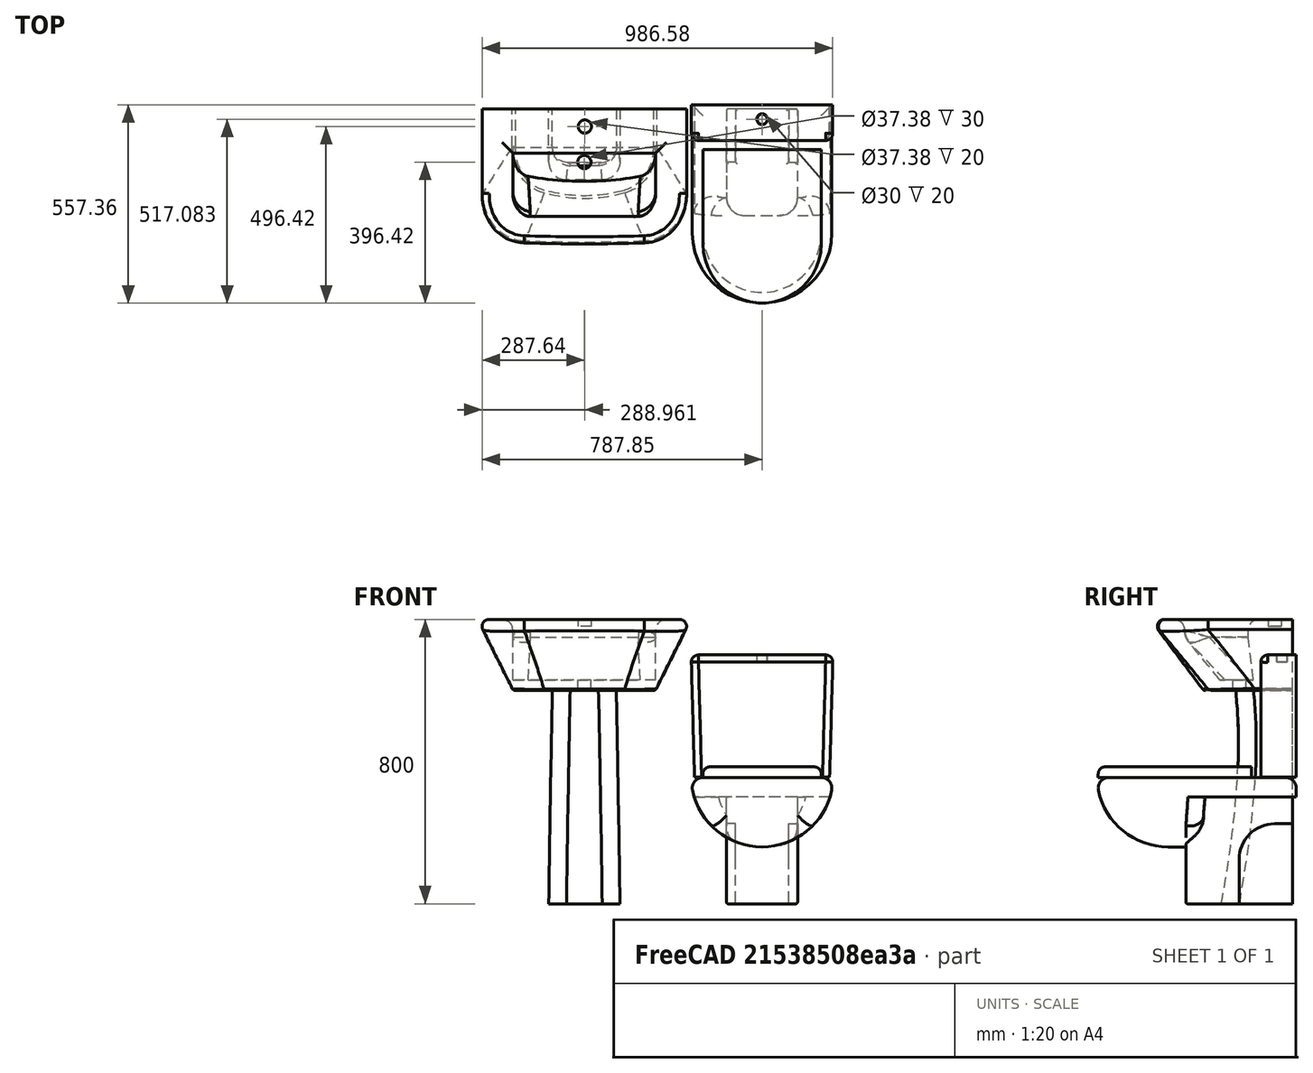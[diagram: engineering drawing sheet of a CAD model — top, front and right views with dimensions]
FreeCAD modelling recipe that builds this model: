
FCSTD DOCUMENT  (FreeCAD 0.16R6706 (Git))
Label: bathroom
License: All rights reserved
LicenseURL: http://en.wikipedia.org/wiki/All_rights_reserved
objects: Part::Fillet×15, Part::Cut×10, Part::Feature×8, Part::Part2DObjectPython×7, Part::Extrusion×6, Part::MultiFuse×4, Part::Loft×3, Part::FeaturePython×2, Part::Mirroring×1
note: 56 computed .brp shape members not serialized (recipe doc carries the construction recipe); baked Part::Feature solids carry a one-line shape summary decoded from their .brp

FEATURE [Part::Cut] Cut
  Placement = pos=(0,0,380) rot=(0,0,1;0rad)
FEATURE [Part::Feature] Extrusion003
  Placement = pos=(0.311371,-200,244.366) rot=(0,0,1;0rad)
  shape: bbox 600 x 300 x 243.1 mm, 6 faces (baked)
FEATURE [Part::Cut] Cut002
  Base = -> Cut
  Tool = -> Extrusion003
FEATURE [Part::Feature] Face
  shape: bbox 399.9 x 2e-07 x 195.3 mm, 1 faces, 0 solids (baked)
FEATURE [Part::Extrusion] Extrusion
  Base = -> Face
  Dir = (0,360.459,0)
  Solid = true
FEATURE [Part::MultiFuse] Fusion
  Placement = pos=(0,0,-400) rot=(0,0,1;0rad)
  Shapes = -> [Cut002,Extrusion]
FEATURE [Part::Cut] Cut003
  Base = -> Fusion
FEATURE [Part::Fillet] Fillet001
  Base = -> Cut003
  Edges = 4 edges r=50: [Edge8,Edge9,Edge15,Edge16]
FEATURE [Part::Part2DObjectPython] Rectangle001  # Draft 2D object (typed FeaturePython)
  ChamferSize = 0
  Columns = 1
  FilletRadius = 0
  Height = 300
  Length = 200
  MakeFace = true
  Placement = pos=(-100,50,0) rot=(0,0,1;0rad)
  Rows = 1
FEATURE [Part::Extrusion] Extrusion004
  Base = -> Rectangle001
  Dir = (0,0,300)
  Solid = true
FEATURE [Part::Fillet] Fillet
  Base = -> Extrusion004
  Edges = 2 edges r=50: [Edge1,Edge2]
FEATURE [Part::Fillet] Fillet002
  Base = -> Fillet001
  Edges = 4 edges r=30: [Edge5,Edge13,Edge21,Edge26]
FEATURE [Part::Fillet] Fillet003
  Base = -> Fillet
  Edges = 2 edges r=5: [Edge17,Edge18]
FEATURE [Part::Part2DObjectPython] Rectangle005  # Draft 2D object (typed FeaturePython)
  ChamferSize = 0
  Columns = 1
  FilletRadius = 0
  Height = 100
  Length = 380
  MakeFace = true
  Placement = pos=(-190,260.943,355.887) rot=(0,0,1;0rad)
  Rows = 1
FEATURE [Part::Part2DObjectPython] Clone2D  label="Clone of Rectangle005 (2D)"  # Draft 2D object (typed FeaturePython)
  Objects = -> [Rectangle005]
  Placement = pos=(-190,260.943,700) rot=(0,0,1;0rad)
  Scale = (1.05,1,1)
FEATURE [Part::Loft] Loft
  Closed = false
  Ruled = false
  Sections = -> [Rectangle005,Clone2D]
  Solid = true
FEATURE [Part::Fillet] Fillet004
  Base = -> Loft
  Edges = 2 edges r=20: [Edge2,Edge4]
FEATURE [Part::Fillet] Fillet005
  Base = -> Fillet004
  Edges = 5 edges r=20: [Edge4,Edge11,Edge13,Edge14,Edge15]
FEATURE [Part::Part2DObjectPython] Rectangle006  # Draft 2D object (typed FeaturePython)
  ChamferSize = 0
  Columns = 1
  FilletRadius = 0
  Height = 200
  Length = 100
  MakeFace = true
  Placement = pos=(200,200,0) rot=(0,0,1;0rad)
  Rows = 1
FEATURE [Part::Extrusion] Extrusion005
  Base = -> Rectangle006
  Dir = (0,0,225)
  Solid = true
FEATURE [Part::Fillet] Fillet006
  Base = -> Extrusion005
  Edges = 1 edges r=100: [Edge4]
  Placement = pos=(-125,0,0) rot=(0,0,1;0rad)
FEATURE [Part::Mirroring] mirror  label="Mirror of Clone of Fillet006"
  Base = (0,500,0)
  Normal = (-1,0,0)
FEATURE [Part::Cut] Cut004
  Base = -> Fillet003
  Tool = -> Fillet006
FEATURE [Part::Cut] Cut005
  Base = -> Cut004
  Tool = -> mirror
FEATURE [Part::Fillet] Fillet007
  Base = -> Cut005
  Edges = 10 edges r=5: [Edge1,Edge2,Edge3,Edge4,Edge5,Edge6,Edge7,Edge8,Edge9,Edge10]
FEATURE [Part::Feature] Wire
  shape: bbox 332.8 x 434.2 x 2e-07 mm, 0 faces, 0 solids (baked)
FEATURE [Part::FeaturePython] Clone001  label="Clone of Wire"  # Draft clone (typed FeaturePython)
  Objects = -> [Wire]
  Placement = pos=(0,0,30) rot=(0,0,1;0rad)
  Scale = (1,1,1)
FEATURE [Part::Loft] Loft001
  Closed = false
  Ruled = false
  Sections = -> [Wire,Clone001]
  Solid = true
FEATURE [Part::Fillet] Fillet008
  Base = -> Loft001
  Edges = 1 edges r=20: [Edge7]
  Placement = pos=(0,970,-50) rot=(0,0,1;0rad)
FEATURE [Part::Part2DObjectPython] Circle  # Draft 2D object (typed FeaturePython)
  FirstAngle = 0
  LastAngle = 0
  MakeFace = true
  Placement = pos=(0.210445,320.663,700) rot=(0,0,1;0rad)
  Radius = 15
FEATURE [Part::Extrusion] Extrusion006
  Base = -> Circle
  Dir = (0,0,20)
  Placement = pos=(0,0,-20) rot=(0,0,1;0rad)
  Solid = true
FEATURE [Part::FeaturePython] Clone  label="Clone of Extrusion006"  # Draft clone (typed FeaturePython)
  Objects = -> [Extrusion006]
  Placement = pos=(0,9.5,-20) rot=(0,0,1;0rad)
  Scale = (0.97,0.97,1)
FEATURE [Part::Cut] Cut006
  Base = -> Fillet005
  Tool = -> Extrusion006
FEATURE [Part::MultiFuse] Fusion001  label="vaso_s"
  Placement = pos=(500,0,0) rot=(0,0,1;0rad)
  Shapes = -> [Cut006,Clone,Fillet008,Fillet007,Fillet002]
FEATURE [Part::Part2DObjectPython] Rectangle007  # Draft 2D object (typed FeaturePython)
  ChamferSize = 0
  Columns = 1
  FilletRadius = 0
  Height = -100
  Length = -400
  MakeFace = true
  Placement = pos=(200,200,0) rot=(0,0,1;0rad)
  Rows = 1
FEATURE [Part::Extrusion] Extrusion007
  Base = -> Rectangle007
  Dir = (0,0,786.749)
  Solid = true
FEATURE [Part::Cut] Cut007
  Tool = -> Extrusion007
FEATURE [Part::Fillet] Fillet009  label="coluna"
  Base = -> Cut007
  Edges = 2 edges r=50: [Edge8,Edge11]
FEATURE [Part::Part2DObjectPython] Rectangle002  # Draft 2D object (typed FeaturePython)
  ChamferSize = 0
  Columns = 1
  FilletRadius = 0
  Height = -400
  Length = 600
  MakeFace = true
  Placement = pos=(-300,100,800) rot=(0,0,1;0rad)
  Rows = 1
FEATURE [Part::Feature] Face001
  Placement = pos=(0,0,600) rot=(0,0,1;0rad)
  shape: bbox 400 x 268.8 x 2e-07 mm, 1 faces, 0 solids (baked)
FEATURE [Part::Loft] Loft002
  Closed = false
  Ruled = false
  Sections = -> [Face001,Rectangle002]
  Solid = true
FEATURE [Part::Fillet] Fillet010
  Base = -> Loft002
  Edges = 2 edges r=150: [Edge2,Edge4]
FEATURE [Part::Fillet] Fillet011
  Base = -> Fillet010
  Edges = 5 edges r=20: [Edge4,Edge11,Edge13,Edge14,Edge15]
FEATURE [Part::Fillet] Fillet012  label="lavat"
  Base = -> Fillet011
  Edges = 5 edges r=10: [Edge3,Edge6,Edge11,Edge12,Edge13]
FEATURE [Part::Feature] Solid
  shape: bbox 402.1 x 200.6 x 205.9 mm, 8 faces (baked)
FEATURE [Part::Feature] Face002
  shape: bbox 402.1 x 178.5 x 0.002 mm, 1 faces, 0 solids (baked)
FEATURE [Part::Extrusion] Extrusion001
  Base = -> Face002
  Dir = (0,0,327.541)
  Solid = true
FEATURE [Part::MultiFuse] Fusion002
  Shapes = -> [Solid,Extrusion001]
FEATURE [Part::Fillet] Fillet013
  Base = -> Fusion002
  Edges = 5 edges r=50: [Edge8,Edge10,Edge14,Edge17,Edge18]
  Placement = pos=(0,0,-170) rot=(0,0,1;0rad)
FEATURE [Part::Cut] Cut001
  Base = -> Fillet012
  Tool = -> Fillet013
FEATURE [Part::Fillet] Fillet014
  Base = -> Cut001
  Edges = 6 edges r=30: [Edge33,Edge34,Edge35,Edge36,Edge37,Edge38]
FEATURE [Part::Feature] Extrusion008
  Placement = pos=(1.32089,450,780) rot=(0,0,1;0rad)
  shape: bbox 37.38 x 37.38 x 68.11 mm, 3 faces (baked)
FEATURE [Part::Cut] Cut008
  Base = -> Fillet014
  Tool = -> Extrusion008
FEATURE [Part::Feature] Extrusion009
  Placement = pos=(0,350,590) rot=(0,0,1;0rad)
  shape: bbox 37.38 x 37.38 x 68.11 mm, 3 faces (baked)
FEATURE [Part::Cut] Cut009
  Base = -> Cut008
  Tool = -> Extrusion009
FEATURE [Part::MultiFuse] Fusion003  label="lavat001"
  Placement = pos=(0,250,0) rot=(0,0,1;0rad)
  Shapes = -> [Fillet009,Cut009]
